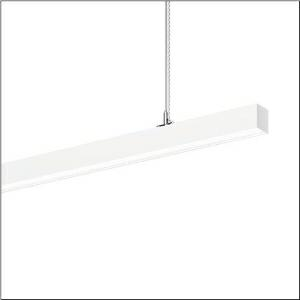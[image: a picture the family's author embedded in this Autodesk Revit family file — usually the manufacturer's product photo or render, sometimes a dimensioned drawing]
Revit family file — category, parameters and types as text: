
# Revit family: silica_21_51mx33dc3dwb
name_source: partatom
category: Lighting Fixtures
units: mm (PartAtom-declared; Revit-internal decimal feet)

## family parameters
Cut with Voids When Loaded = No
Host = Face
Light Source = No
Part Type = Normal
Room Calculation Point = No
Round Connector Dimension = Use Diameter
Shared = No

## types (1)
- --- (1 x LED, 14780 lm, 99.5 W, 3000K)
    Apparent Load = 100 VA
    CIE Flux Codes = 78 96 99 55 100
    Color Rendering = 80
    Color Temperature = 3000K
    Default Elevation = 1800 mm
    Description = Silica 21, office luminaire, primary optical cover: prismatic diffuser, of PMMA, CAT 2 (L<= 3000cd/m²), light emission: direct/indirect distribution, primary light characteristic: symmetric, installation type: suspended mounting, LED, rated luminous flux: 14.780lm, luminous efficacy: 149lm/W, light colour: 830, colour temperature: 3000K, control gear: DALI 2, with terminal, 3+2-pole, max. 2.5mm², mains connection: 220..240V, AC, 50/60Hz, rated input power: 99.5W, luminaire housing, of aluminium, traffic white (RAL 9016), length: 3.004mm, width: 53mm, height: 53mm, protection rating (complete): IP20, insulation class (complete): insulation class I (protective earthing), certification: CE, permissible operating ambient temperature: 0..+35°C, standard: EN 50419, packaging unit: 1 piece
    Height = 53 mm
    Lamp = 1 x LED
    Lamp Light Flux = 14780 lm
    Lamp Power = 99.5 W
    Lamp count = 1
    Length = 3004 mm
    Luminous efficacy = 149 lm/W
    Manufacturer = Siteco
    ModVariant = No
    Model = 51MX33DC3DWB
    Mounting Place = Ceiling
    Mounting Type = Pendant
    Number of Poles = 1
    OnlyDefault = Yes
    Power Factor = 1
    Product Name = Silica 21
    Product group = office luminaire | ceiling pendant
    ProductGroupID = 903
    Protection Class = Protection class I
    Protection Degree = IP 20
    RLX_Detail_Level = 1
    RLX_Emergency_Light_Flux = 0 lm
    RLX_Emergency_Type = 0
    RLX_Emergency_Type_DB = No
    RlxData = <blob elided: 21537 chars, md5=cea01f13>
    Socket = socket
    Standby Power = 0 W
    System Light Flux = 14780 lm
    System Power = 100 W
    Type Comments = factory setting: luminous flux: 100 % | dim-lin: 254 | 345 mA
    Type Image = l_1349007.jpg
    URL = http://relux.com
    VarID = @adj_118961
    Voltage = 0 V
    Weight = 0.00 kg
    Width = 53 mm

## geometry (parser evidence)
native form markers: Blend x4, Sweep x13
no freeform markers — native parametric forms only
